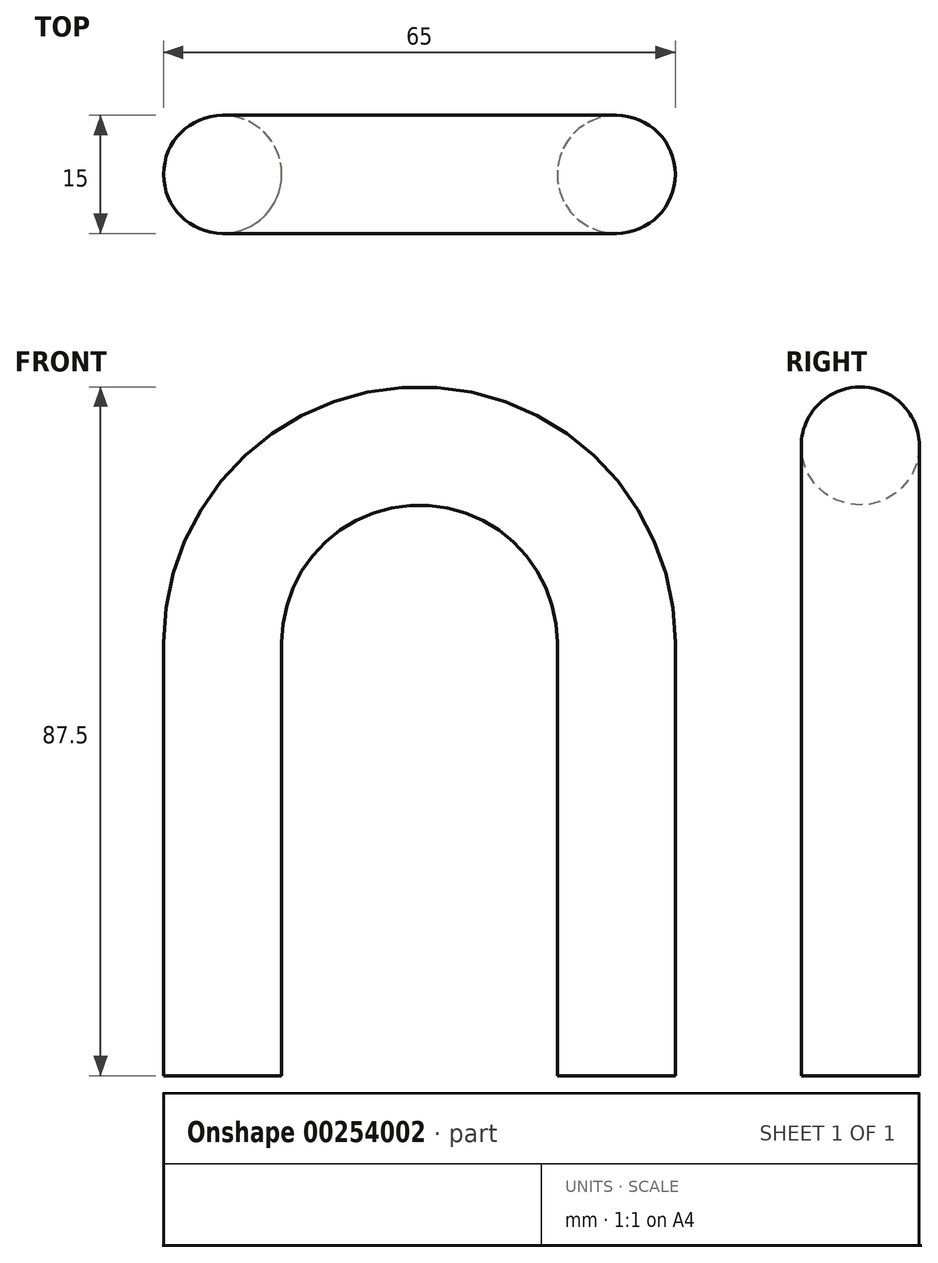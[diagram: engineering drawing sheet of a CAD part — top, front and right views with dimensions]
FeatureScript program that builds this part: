
annotation { "Feature Type Name" : "Feature", "Feature Type Description" : "" }
export const myFeature = defineFeature(function(context is Context, id is Id, definition is map)
    precondition{}
    {
        {
            var Q0;
            Q0=qCreatedBy(makeId("Front.planeOp"),FACE);
            var sketch = newSketch(context, id + "F0", { "sketchPlane" : qUnion([Q0])});
            skLineSegment(sketch, "E0", {"start": v(25, 0) * mm, "end": v(25, 55) * mm});
            skArc(sketch, "E1", {"start": v(25, 55) * mm, "mid": v(0, 80) * mm, "end": v(-25, 55) * mm});
            skLineSegment(sketch, "E2", {"start": v(-25, 55) * mm, "end": v(-25, 0) * mm});
            skSolve(sketch);
        }
        {
            var Q0;
            Q0=qCreatedBy(makeId("Top.planeOp"),FACE);
            var sketch = newSketch(context, id + "F1", { "sketchPlane" : qUnion([Q0])});
            skCircle(sketch, "E3", {"center": v(25, 0) * mm, "radius": 7.5 * mm});
            skSolve(sketch);
        }
        {
            var Q0;
            Q0=makeQuery(id+"F1.imprint","IMPRINT",FACE,{"disambiguationData":[TD([[makeQuery(id+"F1.imprint","IMPRINT",EDGE,{"derivedFrom":sQuery(id+"F1.wireOp",EDGE,"E3")}),1.0]])]});
            var Q1;
            Q1 = qConstructionFilter(qBodyType(qCreatedBy(id + "F0" ,EDGE), BodyType.WIRE), ConstructionObject.NO);
            sweep(context, id + "F2", {"profiles" : qUnion([Q0]), "path" : qUnion([Q1])});
        }
    });
